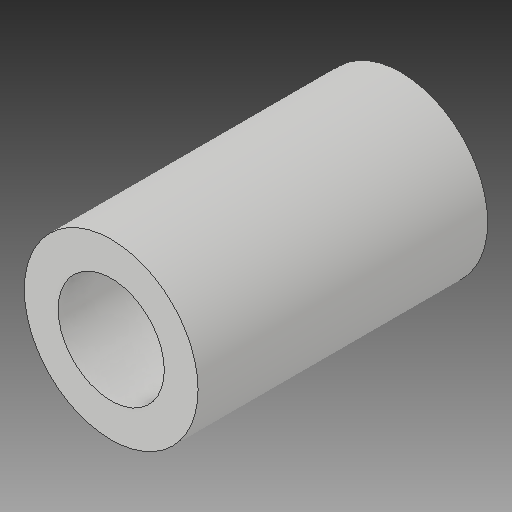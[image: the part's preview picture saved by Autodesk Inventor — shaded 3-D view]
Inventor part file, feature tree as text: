
AUTODESK INVENTOR PART (.ipt)
format: ipt  version: 2018 (Build 220112000, 112)  size: 105,984 bytes
history: native  units: mm
features: other x3, sketch x1
ambient origin geometry x8: Origin, YZ Plane, XZ Plane, XY Plane, X Axis, Y Axis, Z Axis, Center Point
bodies: Solid1 (feature_tree)
feature tree (4):
  other  "Long-Spacer_MIR.ipt"
  other  "Solid1::Long-Spacer_MIR.ipt"
  other  "TaggingFeature1"
  sketch  "Sketch1"  dims[d0=10.0mm]
